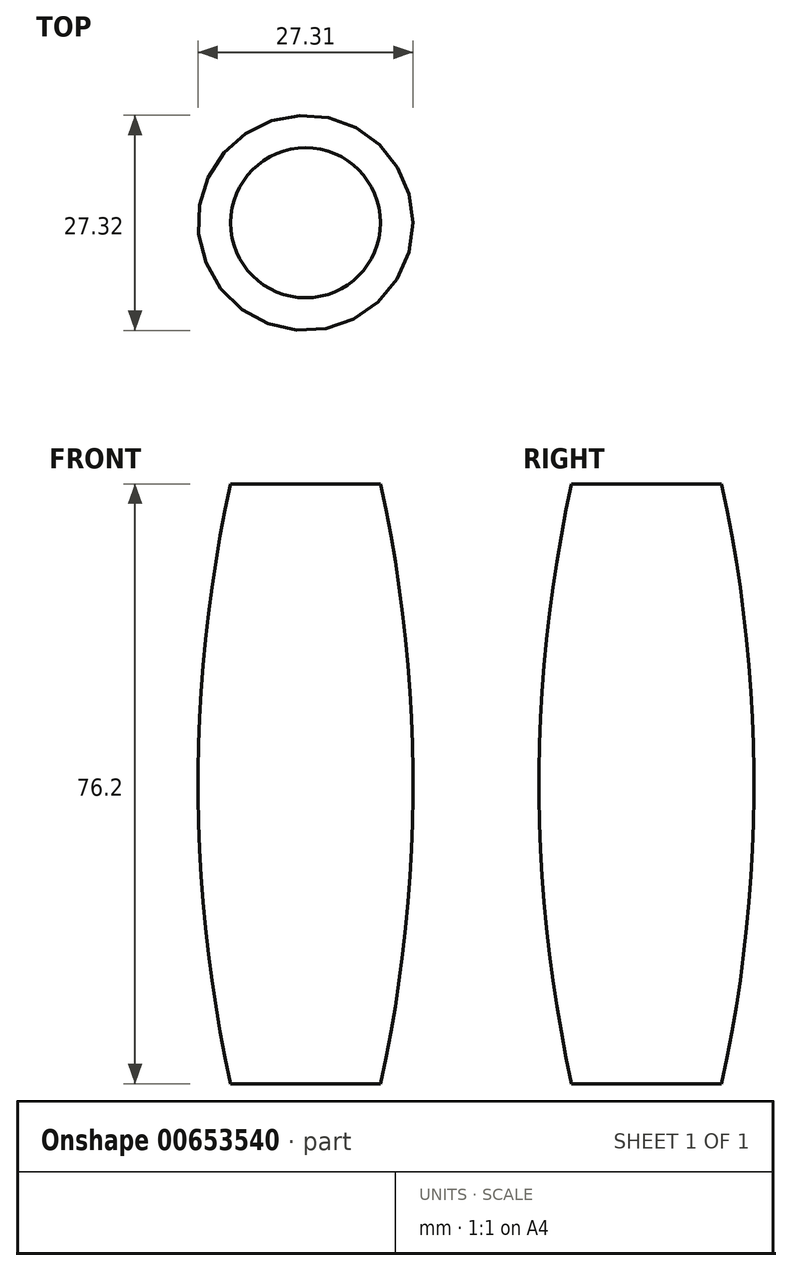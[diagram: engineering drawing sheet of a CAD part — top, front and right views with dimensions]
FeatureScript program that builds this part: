
annotation { "Feature Type Name" : "Feature", "Feature Type Description" : "" }
export const myFeature = defineFeature(function(context is Context, id is Id, definition is map)
    precondition{}
    {
        {
            var Q0;
            Q0=qCreatedBy(makeId("Front.planeOp"),FACE);
            var sketch = newSketch(context, id + "F0", { "sketchPlane" : qUnion([Q0])});
            skArc(sketch, "E0", {"start": v(0, 76.2) * mm, "mid": v(-4.13, 38.1) * mm, "end": v(0, 0) * mm});
            skLineSegment(sketch, "E1", {"start": v(0, 0) * mm, "end": v(19.05, 0) * mm});
            skLineSegment(sketch, "E2", {"start": v(0, 76.2) * mm, "end": v(19.05, 76.2) * mm});
            skArc(sketch, "E3", {"start": v(19.05, 0) * mm, "mid": v(23.18, 38.1) * mm, "end": v(19.05, 76.2) * mm});
            skLineSegment(sketch, "E4", {"start": v(9.52, 76.2) * mm, "end": v(9.53, 0) * mm});
            skSolve(sketch);
        }
        {
            var Q0;
            {var subQ0=sQuery(id+"F0.wireOp",EDGE,"E0");Q0=makeQuery(id+"F0.imprint","IMPRINT",FACE,{"disambiguationData":[TD([[makeQuery(id+"F0.imprint","IMPRINT",EDGE,{"derivedFrom":subQ0}),1.0]])]});}
            var Q1;
            Q1=sQuery(id+"F0.wireOp",EDGE,"E4");
            revolve(context, id + "F1", {"entities" : qUnion([Q0]), "axis" : qUnion([Q1]), "revolveType" : RevolveType.FULL});
        }
    });
